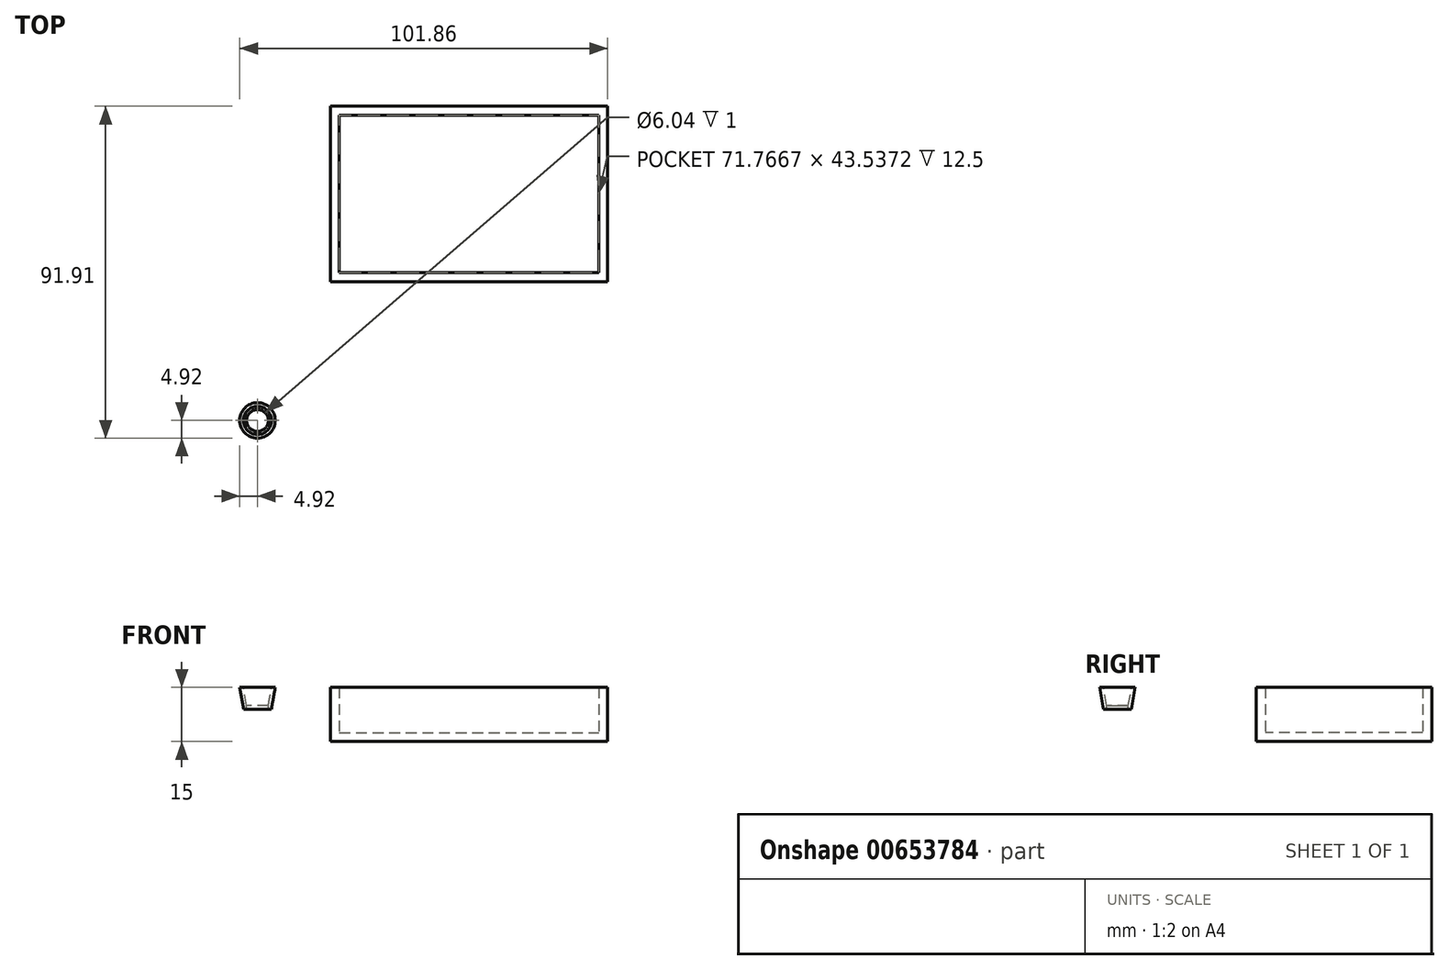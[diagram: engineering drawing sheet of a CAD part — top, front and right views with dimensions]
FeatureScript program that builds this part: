
annotation { "Feature Type Name" : "Feature", "Feature Type Description" : "" }
export const myFeature = defineFeature(function(context is Context, id is Id, definition is map)
    precondition{}
    {
        {
            var Q0;
            Q0=qCreatedBy(makeId("Top.planeOp"),FACE);
            var sketch = newSketch(context, id + "F0", { "sketchPlane" : qUnion([Q0])});
            skLineSegment(sketch, "E0.bottom", {"start": v(-49.33, 16.45) * mm, "end": v(27.43, 16.45) * mm});
            skLineSegment(sketch, "E0.top", {"start": v(-49.33, -32.09) * mm, "end": v(27.43, -32.09) * mm});
            skLineSegment(sketch, "E0.left", {"start": v(-49.33, 16.45) * mm, "end": v(-49.33, -32.09) * mm});
            skLineSegment(sketch, "E0.right", {"start": v(27.43, 16.45) * mm, "end": v(27.43, -32.09) * mm});
            skCircle(sketch, "E1", {"center": v(-19.5, -10.54) * mm, "radius": 3.9 * mm});
            skSolve(sketch);
        }
        {
            var Q0;
            Q0=makeQuery(id+"F0.imprint","IMPRINT",FACE,{"disambiguationData":[TD([[makeQuery(id+"F0.imprint","IMPRINT",EDGE,{"derivedFrom":sQuery(id+"F0.wireOp",EDGE,"E0.bottom")}),-1.0]])]});
            var Q1;
            Q1=makeQuery(id+"F0.imprint","IMPRINT",FACE,{"disambiguationData":[TD([[makeQuery(id+"F0.imprint","IMPRINT",EDGE,{"derivedFrom":sQuery(id+"F0.wireOp",EDGE,"E1")}),1.0]])]});
            extrude(context, id + "F1", {"entities" : qUnion([Q0, Q1]), "depth" : 15 * mm, "offsetDistance" : 25 * mm});
        }
        {
            var Q0;
            Q0=makeQuery(id+"F1.opExtrude","CAP_FACE",FACE,{"disambiguationData":[OSD([sQuery(id+"F0.wireOp",EDGE,"E0.bottom"),sQuery(id+"F0.wireOp",EDGE,"E0.top"),sQuery(id+"F0.wireOp",EDGE,"E0.left"),sQuery(id+"F0.wireOp",EDGE,"E0.right")])],"isStart":false});
            shell(context, id + "F2", {"entities" : qUnion([Q0]), "thickness" : 2.5 * mm});
        }
        {
            var Q0;
            Q0=makeQuery(id+"F1.opExtrude","CAP_FACE",FACE,{"disambiguationData":[OSD([sQuery(id+"F0.wireOp",EDGE,"E0.bottom"),sQuery(id+"F0.wireOp",EDGE,"E0.top"),sQuery(id+"F0.wireOp",EDGE,"E0.left"),sQuery(id+"F0.wireOp",EDGE,"E0.right")])],"isStart":false});
            var sketch = newSketch(context, id + "F3", { "sketchPlane" : qUnion([Q0])});
            skLineSegment(sketch, "E2.0.0", {"start": v(-46.83, 13.95) * mm, "end": v(-46.83, -29.59) * mm});
            skLineSegment(sketch, "E2.0.1", {"start": v(-46.83, -29.59) * mm, "end": v(24.93, -29.59) * mm});
            skLineSegment(sketch, "E2.0.2", {"start": v(24.93, -29.59) * mm, "end": v(24.93, 13.95) * mm});
            skLineSegment(sketch, "E2.0.3", {"start": v(24.93, 13.95) * mm, "end": v(-46.83, 13.95) * mm});
            skCircle(sketch, "E3.0", {"center": v(-19.5, -10.54) * mm, "radius": 3.9 * mm});
            skSolve(sketch);
        }
        {
            var Q0;
            Q0=makeQuery(id+"F1.opExtrude","SWEPT_BODY",BODY,{"disambiguationData":[OSD([sQuery(id+"F0.wireOp",EDGE,"E0.bottom"),sQuery(id+"F0.wireOp",EDGE,"E0.top"),sQuery(id+"F0.wireOp",EDGE,"E0.left"),sQuery(id+"F0.wireOp",EDGE,"E0.right")])]});
            transform(context, id + "F4", {"entities" : qUnion([Q0]), "transformType" : TransformType.TRANSLATION_3D, "dx" : 50 * mm, "dy" : 60 * mm, "dz" : 0 * mm, "makeCopy" : false});
        }
        {
            var Q0;
            Q0=makeQuery(id+"F3.imprint","IMPRINT",FACE,{"disambiguationData":[TD([[makeQuery(id+"F3.imprint","IMPRINT",EDGE,{"derivedFrom":sQuery(id+"F3.wireOp",EDGE,"E3.0")}),1.0]])]});
            extrude(context, id + "F5", {"entities" : qUnion([Q0]), "oppositeDirection" : true, "depth" : 5 * mm, "offsetDistance" : 25 * mm, "hasDraft" : true, "draftAngle" : 10 * degree, "draftPullDirection" : true});
        }
        {
            var Q0;
            Q0=makeQuery(id+"F5.opExtrude","CAP_FACE",FACE,{"disambiguationData":[OSD([sQuery(id+"F3.wireOp",EDGE,"E3.0")])],"isStart":true});
            shell(context, id + "F6", {"entities" : qUnion([Q0]), "thickness" : 1 * mm, "oppositeDirection" : true});
        }
        {
            var Q0;
            {var subQ0=sQuery(id+"F3.wireOp",EDGE,"E3.0");Q0=makeQuery(id+"F6.opShell","OFFSET_FACE",FACE,{"disambiguationData":[OSD([subQ0]),TDD([makeQuery(id+"F5.opExtrude","CAP_FACE",FACE,{"disambiguationData":[OSD([subQ0])],"isStart":false})])]});}
            extrude(context, id + "F7", {"entities" : qUnion([Q0]), "operationType" : NewBodyOperationType.REMOVE, "endBound" : BoundingType.UP_TO_NEXT, "oppositeDirection" : true, "depth" : 25 * mm, "offsetDistance" : 25 * mm});
        }
    });
